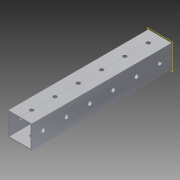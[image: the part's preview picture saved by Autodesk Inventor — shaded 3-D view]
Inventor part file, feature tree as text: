
AUTODESK INVENTOR PART (.ipt)
format: ipt  version: 2014 (Build 180170000, 170)  size: 1,239,040 bytes
history: native  units: in
note: dims shown in document units (in); Inventor stores cm internally (conversion verified against a paired STEP export)
features: extrude x2, sketch x2, pattern_circular x1, other x1, plane x1, imported_body x1
ambient origin geometry x8: Origin, YZ Plane, XZ Plane, XY Plane, X Axis, Y Axis, Z Axis, Center Point
bodies: Body1 (feature_tree)
feature tree (8):
  pattern_circular  "CirPattern2"
  other  "217-3426-STEP1"
  plane  "Work Plane1"
  extrude  "Extrusion1"  Depth=393.7008in TaperAngle=0.0deg
  extrude  "Extrusion4"  Depth=0.5in
  imported_body  "Base1"
  sketch  "Sketch1"  dims[d0=-6.0in d1=393.7008in d2=0.0in]
  sketch  "Sketch4"  dims[d16=0.5in d17=0.5in d18=3.937in d19=0.0in]
